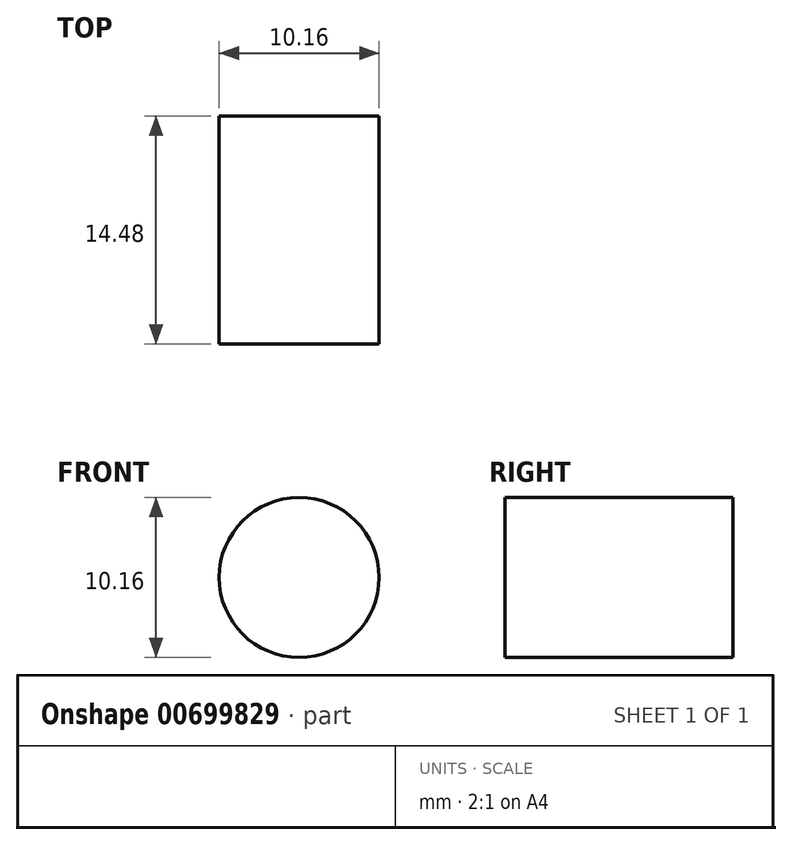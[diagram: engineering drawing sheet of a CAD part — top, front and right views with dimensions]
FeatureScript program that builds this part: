
annotation { "Feature Type Name" : "Feature", "Feature Type Description" : "" }
export const myFeature = defineFeature(function(context is Context, id is Id, definition is map)
    precondition{}
    {
        {
            var Q0;
            Q0=qCreatedBy(makeId("Front.planeOp"),FACE);
            var sketch = newSketch(context, id + "F0", { "sketchPlane" : qUnion([Q0])});
            skCircle(sketch, "E0", {"center": v(0, 0) * mm, "radius": 5.08 * mm});
            skSolve(sketch);
        }
        {
            var Q0;
            Q0=qSketchRegion(id+"F0",true);
            extrude(context, id + "F1", {"entities" : qUnion([Q0]), "depth" : 14.48 * mm});
        }
    });
